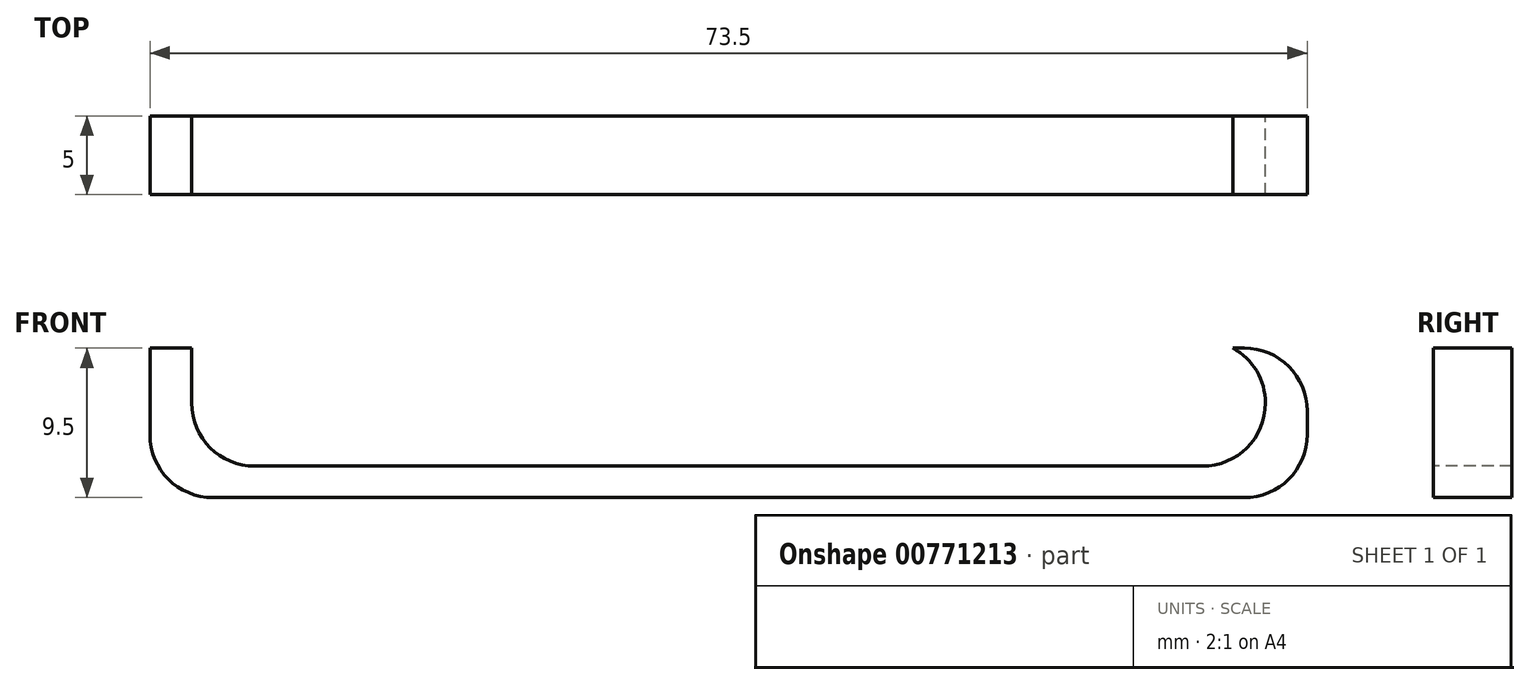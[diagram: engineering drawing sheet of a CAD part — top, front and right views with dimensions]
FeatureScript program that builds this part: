
annotation { "Feature Type Name" : "Feature", "Feature Type Description" : "" }
export const myFeature = defineFeature(function(context is Context, id is Id, definition is map)
    precondition{}
    {
        {
            var Q0;
            Q0=qCreatedBy(makeId("Top.planeOp"),FACE);
            var sketch = newSketch(context, id + "F0", { "sketchPlane" : qUnion([Q0])});
            skLineSegment(sketch, "E0.bottom", {"start": v(36.75, 2.5) * mm, "end": v(-36.75, 2.5) * mm});
            skLineSegment(sketch, "E0.top", {"start": v(36.75, -2.5) * mm, "end": v(-36.75, -2.5) * mm});
            skLineSegment(sketch, "E0.left", {"start": v(36.75, 2.5) * mm, "end": v(36.75, -2.5) * mm});
            skLineSegment(sketch, "E0.right", {"start": v(-36.75, 2.5) * mm, "end": v(-36.75, -2.5) * mm});
            skPoint(sketch, "E0.middle", {"position": v(0, 0) * mm});
            skSolve(sketch);
        }
        {
            var Q0;
            Q0=makeQuery(id+"F0.imprint","IMPRINT",FACE,{"disambiguationData":[TD([[makeQuery(id+"F0.imprint","IMPRINT",EDGE,{"derivedFrom":sQuery(id+"F0.wireOp",EDGE,"E0.bottom")}),1.0]])]});
            extrude(context, id + "F1", {"entities" : qUnion([Q0]), "depth" : 10 * mm, "offsetDistance" : 25 * mm});
        }
        {
            var Q0;
            Q0=makeQuery(id+"F1.opExtrude","CAP_FACE",FACE,{"disambiguationData":[OSD([sQuery(id+"F0.wireOp",EDGE,"E0.bottom"),sQuery(id+"F0.wireOp",EDGE,"E0.top"),sQuery(id+"F0.wireOp",EDGE,"E0.left"),sQuery(id+"F0.wireOp",EDGE,"E0.right")])],"isStart":false});
            var sketch = newSketch(context, id + "F2", { "sketchPlane" : qUnion([Q0])});
            skLineSegment(sketch, "E1.bottom", {"start": v(34.1, 2.5) * mm, "end": v(-34.1, 2.5) * mm});
            skLineSegment(sketch, "E1.top", {"start": v(34.1, -2.5) * mm, "end": v(-34.1, -2.5) * mm});
            skLineSegment(sketch, "E1.left", {"start": v(34.1, 2.5) * mm, "end": v(34.1, -2.5) * mm});
            skLineSegment(sketch, "E1.right", {"start": v(-34.1, 2.5) * mm, "end": v(-34.1, -2.5) * mm});
            skPoint(sketch, "E1.middle", {"position": v(0, 0) * mm});
            skSolve(sketch);
        }
        {
            var Q0;
            Q0=makeQuery(id+"F2.imprint","IMPRINT",FACE,{"disambiguationData":[TD([[makeQuery(id+"F2.imprint","IMPRINT",EDGE,{"derivedFrom":sQuery(id+"F2.wireOp",EDGE,"E1.bottom")}),1.0]])]});
            extrude(context, id + "F3", {"entities" : qUnion([Q0]), "operationType" : NewBodyOperationType.REMOVE, "oppositeDirection" : true, "depth" : 8 * mm, "offsetDistance" : 25 * mm});
        }
        {
            var Q0;
            Q0=makeQuery(id+"F3.boolean.opBoolean","COPY",EDGE,{"derivedFrom":makeQuery(id+"F3.opExtrude","CAP_EDGE",EDGE,{"disambiguationData":[OSD([sQuery(id+"F2.wireOp",EDGE,"E1.left")])],"isStart":false})});
            var Q1;
            Q1=makeQuery(id+"F3.boolean.opBoolean","COPY",EDGE,{"derivedFrom":makeQuery(id+"F3.opExtrude","CAP_EDGE",EDGE,{"disambiguationData":[OSD([sQuery(id+"F2.wireOp",EDGE,"E1.right")])],"isStart":false})});
            fillet(context, id + "F4", {"entities" : qUnion([Q0, Q1]), "radius" : 4 * mm, "tangentPropagation" : true, "allowEdgeOverflow" : false});
        }
        {
            var Q0;
            {var subQ0=sQuery(id+"F0.wireOp",EDGE,"E0.bottom");var subQ1=sQuery(id+"F0.wireOp",EDGE,"E0.right");var subQ2=sQuery(id+"F0.wireOp",EDGE,"E0.top");Q0=makeQuery(id+"F3.boolean.opBoolean","SPLIT",FACE,{"disambiguationData":[TD([makeQuery(id+"F1.opExtrude","SWEPT_FACE",FACE,{"disambiguationData":[OSD([subQ1])]})])],"derivedFrom":makeQuery(id+"F1.opExtrude","CAP_FACE",FACE,{"disambiguationData":[OSD([subQ0,subQ2,sQuery(id+"F0.wireOp",EDGE,"E0.left"),subQ1])],"isStart":false})});}
            extrude(context, id + "F5", {"entities" : qUnion([Q0]), "operationType" : NewBodyOperationType.ADD, "depth" : 2 * mm, "offsetDistance" : 25 * mm});
        }
        {
            var Q0;
            {var subQ0=sQuery(id+"F2.wireOp",EDGE,"E1.right");Q0=makeQuery(id+"F5.boolean.opBoolean","MERGE",FACE,{"derivedFrom":[makeQuery(id+"F3.boolean.opBoolean","COPY",FACE,{"derivedFrom":makeQuery(id+"F3.opExtrude","SWEPT_FACE",FACE,{"disambiguationData":[OSD([subQ0])]})}),makeQuery(id+"F5.opExtrude","SWEPT_FACE",FACE,{"disambiguationData":[OSD([subQ0])]})]});}
            var sketch = newSketch(context, id + "F6", { "sketchPlane" : qUnion([Q0])});
            skLineSegment(sketch, "E2.bottom", {"start": v(-2.5, 12) * mm, "end": v(2.5, 12) * mm});
            skLineSegment(sketch, "E2.top", {"start": v(-2.5, 10) * mm, "end": v(2.5, 10) * mm});
            skLineSegment(sketch, "E2.left", {"start": v(-2.5, 12) * mm, "end": v(-2.5, 10) * mm});
            skLineSegment(sketch, "E2.right", {"start": v(2.5, 12) * mm, "end": v(2.5, 10) * mm});
            skSolve(sketch);
        }
        {
            var Q0;
            Q0=makeQuery(id+"F6.imprint","IMPRINT",FACE,{"disambiguationData":[TD([[makeQuery(id+"F6.imprint","IMPRINT",EDGE,{"derivedFrom":sQuery(id+"F6.wireOp",EDGE,"E2.bottom")}),1.0]])]});
            extrude(context, id + "F7", {"entities" : qUnion([Q0]), "operationType" : NewBodyOperationType.ADD, "depth" : 76.5 * mm, "offsetDistance" : 25 * mm});
        }
        {
            var Q0;
            Q0=makeQuery(id+"F7.opExtrude","CAP_EDGE",EDGE,{"disambiguationData":[OSD([sQuery(id+"F6.wireOp",EDGE,"E2.top")])],"isStart":true});
            var Q1;
            Q1=makeQuery(id+"F3.boolean.opBoolean","COPY",EDGE,{"derivedFrom":makeQuery(id+"F3.opExtrude","CAP_EDGE",EDGE,{"disambiguationData":[OSD([sQuery(id+"F2.wireOp",EDGE,"E1.left")])],"isStart":true})});
            fillet(context, id + "F8", {"entities" : qUnion([Q0, Q1]), "radius" : 4 * mm, "tangentPropagation" : true, "allowEdgeOverflow" : false});
        }
        {
            var Q0;
            Q0=makeQuery(id+"F7.boolean.opBoolean","MERGE",FACE,{"derivedFrom":[makeQuery(id+"F5.opExtrude","CAP_FACE",FACE,{"disambiguationData":[OSD([sQuery(id+"F0.wireOp",EDGE,"E0.bottom"),sQuery(id+"F0.wireOp",EDGE,"E0.top"),sQuery(id+"F0.wireOp",EDGE,"E0.left"),sQuery(id+"F0.wireOp",EDGE,"E0.right")])],"isStart":false}),makeQuery(id+"F7.opExtrude","SWEPT_FACE",FACE,{"disambiguationData":[OSD([sQuery(id+"F6.wireOp",EDGE,"E2.bottom")])]})]});
            extrude(context, id + "F9", {"entities" : qUnion([Q0]), "operationType" : NewBodyOperationType.REMOVE, "oppositeDirection" : true, "depth" : 2.5 * mm, "offsetDistance" : 25 * mm});
        }
        {
            var Q0;
            Q0=makeQuery(id+"F1.opExtrude","CAP_EDGE",EDGE,{"disambiguationData":[OSD([sQuery(id+"F0.wireOp",EDGE,"E0.left")])],"isStart":true});
            var Q1;
            Q1=makeQuery(id+"F9.boolean.opBoolean","COPY",EDGE,{"derivedFrom":makeQuery(id+"F9.opExtrude","CAP_EDGE",EDGE,{"disambiguationData":[OSD([sQuery(id+"F0.wireOp",EDGE,"E0.right")])],"isStart":false})});
            var Q2;
            Q2=makeQuery(id+"F1.opExtrude","CAP_EDGE",EDGE,{"disambiguationData":[OSD([sQuery(id+"F0.wireOp",EDGE,"E0.right")])],"isStart":true});
            var Q3;
            {var subQ0=sQuery(id+"F0.wireOp",EDGE,"E0.left");Q3=makeQuery(id+"F9.boolean.opBoolean","INTERSECT",EDGE,{"derivedFrom":[makeQuery(id+"F1.opExtrude","SWEPT_FACE",FACE,{"disambiguationData":[OSD([subQ0])]}),makeQuery(id+"F9.opExtrude","CAP_FACE",FACE,{"disambiguationData":[OSD([sQuery(id+"F0.wireOp",EDGE,"E0.bottom"),sQuery(id+"F0.wireOp",EDGE,"E0.top"),subQ0,sQuery(id+"F0.wireOp",EDGE,"E0.right"),sQuery(id+"F6.wireOp",EDGE,"E2.bottom")])],"isStart":false})]});}
            fillet(context, id + "F10", {"entities" : qUnion([Q0, Q1, Q2, Q3]), "radius" : 4 * mm, "tangentPropagation" : true, "allowEdgeOverflow" : false});
        }
    });
